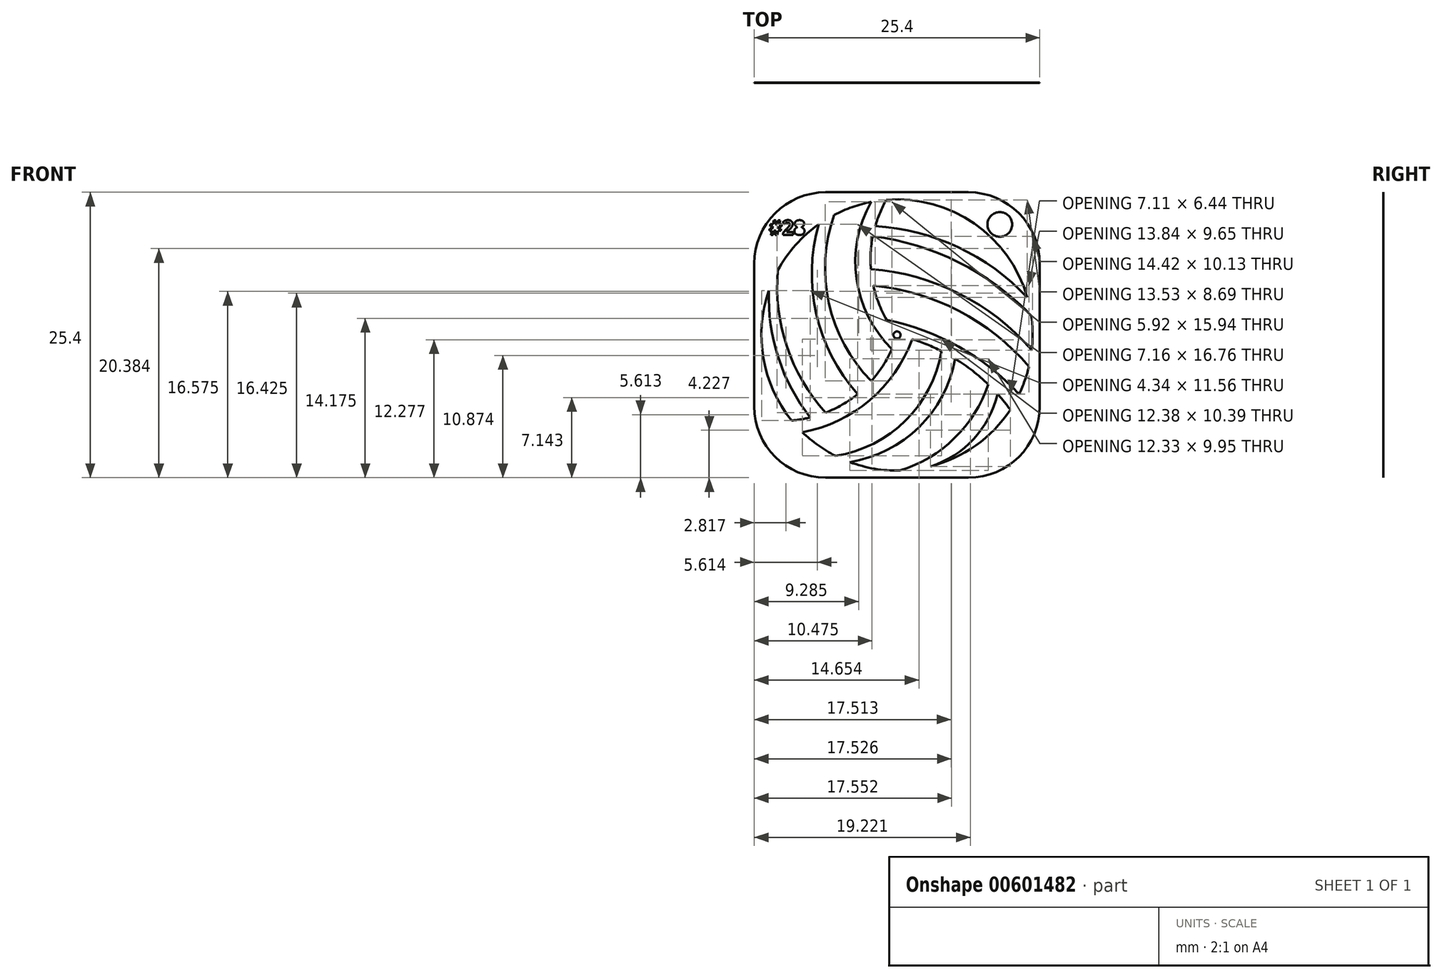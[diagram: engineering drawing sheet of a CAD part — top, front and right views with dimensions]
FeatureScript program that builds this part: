
annotation { "Feature Type Name" : "Feature", "Feature Type Description" : "" }
export const myFeature = defineFeature(function(context is Context, id is Id, definition is map)
    precondition{}
    {
        {
            var Q0;
            Q0=qCreatedBy(makeId("Front.planeOp"),FACE);
            var sketch = newSketch(context, id + "F0", { "sketchPlane" : qUnion([Q0])});
            skLineSegment(sketch, "E0", {"start": v(0, 6.35) * mm, "end": v(0, 19.05) * mm});
            skLineSegment(sketch, "E1", {"start": v(6.35, 0) * mm, "end": v(19.05, 0) * mm});
            skLineSegment(sketch, "E2", {"start": v(25.4, 6.35) * mm, "end": v(25.4, 19.05) * mm});
            skLineSegment(sketch, "E3", {"start": v(19.05, 25.4) * mm, "end": v(6.35, 25.4) * mm});
            skCircle(sketch, "E4", {"center": v(12.7, 12.7) * mm, "radius": 12.07 * mm});
            skPoint(sketch, "E5.visualSharp", {"position": v(0, 25.4) * mm});
            skArc(sketch, "E5.filletArc", {"start": v(6.35, 25.4) * mm, "mid": v(1.86, 23.54) * mm, "end": v(0, 19.05) * mm});
            skPoint(sketch, "E6.visualSharp", {"position": v(0, 0) * mm});
            skArc(sketch, "E6.filletArc", {"start": v(0, 6.35) * mm, "mid": v(1.86, 1.86) * mm, "end": v(6.35, 0) * mm});
            skPoint(sketch, "E7.visualSharp", {"position": v(25.4, 0) * mm});
            skArc(sketch, "E7.filletArc", {"start": v(19.05, 0) * mm, "mid": v(23.54, 1.86) * mm, "end": v(25.4, 6.35) * mm});
            skPoint(sketch, "E8.visualSharp", {"position": v(25.4, 25.4) * mm});
            skArc(sketch, "E8.filletArc", {"start": v(25.4, 19.05) * mm, "mid": v(23.54, 23.54) * mm, "end": v(19.05, 25.4) * mm});
            skPoint(sketch, "E9.centerSnap0", {"position": v(23.54, 23.54) * mm});
            skCircle(sketch, "E10", {"center": v(21.84, 22.54) * mm, "radius": 1.1 * mm});
            skPoint(sketch, "E9.center.orphan", {"position": v(21.97, 23.54) * mm});
            skArc(sketch, "E11", {"start": v(11.75, 24.73) * mm, "mid": v(10.37, 18.57) * mm, "end": v(12.7, 12.7) * mm});
            skArc(sketch, "E12", {"start": v(22.78, 6.06) * mm, "mid": v(18.34, 10.3) * mm, "end": v(12.7, 12.7) * mm});
            skArc(sketch, "E13", {"start": v(3.33, 5.1) * mm, "mid": v(9.2, 7.45) * mm, "end": v(12.7, 12.7) * mm});
            skLineSegment(sketch, "E14", {"start": v(15.68, 24.4) * mm, "end": v(15.68, 24.4) * mm});
            skPoint(sketch, "E15.start.orphan", {"position": v(19.05, 22.96) * mm});
            skArc(sketch, "E16", {"start": v(7.22, 1.95) * mm, "mid": v(13.45, 5.08) * mm, "end": v(16.67, 11.26) * mm});
            skArc(sketch, "E17", {"start": v(12.96, 0.64) * mm, "mid": v(17.81, 3.52) * mm, "end": v(20.82, 8.3) * mm});
            skArc(sketch, "E18", {"start": v(24.43, 9.9) * mm, "mid": v(18.2, 14.84) * mm, "end": v(10.6, 17.1) * mm});
            skArc(sketch, "E19", {"start": v(24.64, 14.44) * mm, "mid": v(18.2, 19.17) * mm, "end": v(10.54, 21.5) * mm});
            skArc(sketch, "E20", {"start": v(7.1, 23.4) * mm, "mid": v(6.64, 15.53) * mm, "end": v(10.4, 8.6) * mm});
            skArc(sketch, "E21", {"start": v(2.1, 18.46) * mm, "mid": v(2.9, 11.68) * mm, "end": v(6.35, 5.8) * mm});
            skArc(sketch, "E22", {"start": v(10.4, 24.54) * mm, "mid": v(9.1, 17.69) * mm, "end": v(12.25, 11.46) * mm});
            skArc(sketch, "E23", {"start": v(5.74, 22.56) * mm, "mid": v(5.52, 14.56) * mm, "end": v(9.2, 7.45) * mm});
            skArc(sketch, "E24", {"start": v(1.3, 16.65) * mm, "mid": v(2.14, 10.68) * mm, "end": v(4.99, 5.36) * mm});
            skArc(sketch, "E25", {"start": v(23.56, 7.45) * mm, "mid": v(18.19, 11.67) * mm, "end": v(11.78, 14.04) * mm});
            skArc(sketch, "E26", {"start": v(24.7, 11.36) * mm, "mid": v(18.24, 16.38) * mm, "end": v(10.37, 18.57) * mm});
            skArc(sketch, "E27", {"start": v(4.28, 4.05) * mm, "mid": v(10.27, 6.9) * mm, "end": v(14.04, 12.34) * mm});
            skArc(sketch, "E28", {"start": v(8.49, 1.4) * mm, "mid": v(14.65, 4.5) * mm, "end": v(17.87, 10.59) * mm});
            skArc(sketch, "E29", {"start": v(15.67, 1) * mm, "mid": v(19.5, 3.44) * mm, "end": v(21.65, 7.45) * mm});
            skPoint(sketch, "E30.start.orphan", {"position": v(24.3, 16.04) * mm});
            skArc(sketch, "E31", {"start": v(24.3, 16.04) * mm, "mid": v(18.13, 20.5) * mm, "end": v(10.76, 22.38) * mm});
            skCircle(sketch, "E32", {"center": v(12.7, 12.7) * mm, "radius": 0.32 * mm});
            skText(sketch, "E33", { "text": "#28", "fontName": "OpenSans-Bold.ttf"});
            skLineSegment(sketch, "E34", {"start": v(0.36, 21.14) * mm, "end": v(0.36, 5.6) * mm});
            skLineSegment(sketch, "E35", {"start": v(0.36, 17.45) * mm, "end": v(0, 17.45) * mm});
            const initialGuessF0  = {"E33": [0.00131, 0.02162, 1, 0, 0.0013]};
            skSetInitialGuess(sketch, initialGuessF0);
            skSolve(sketch);
        }
        {
            var Q0;
            Q0=qSketchRegion(id+"F0",true);
            extrude(context, id + "F1", {"entities" : qUnion([Q0]), "depth" : 1 / 203.2 * mm, "offsetDistance" : 25.4 * mm});
        }
        {
            var Q0;
            Q0=qSketchRegion(id+"F0",true);
            var Q1;
            {var subQ0=sQuery(id+"F0.wireOp",EDGE,"E20");Q1=makeQuery(id+"F0.imprint","IMPRINT",FACE,{"disambiguationData":[TD([[makeQuery(id+"F0.imprint","IMPRINT",EDGE,{"derivedFrom":subQ0}),-1.0]])]});}
            var Q2;
            {var subQ0=sQuery(id+"F0.wireOp",EDGE,"E21");Q2=makeQuery(id+"F0.imprint","IMPRINT",FACE,{"disambiguationData":[TD([[makeQuery(id+"F0.imprint","IMPRINT",EDGE,{"derivedFrom":subQ0}),-1.0]])]});}
            var Q3;
            {var subQ3=sQuery(id+"F0.wireOp",EDGE,"E22");Q3=makeQuery(id+"F0.imprint","IMPRINT",FACE,{"disambiguationData":[TD([[makeQuery(id+"F0.imprint","IMPRINT",EDGE,{"derivedFrom":subQ3}),1.0]])]});}
            var Q4;
            {var subQ5=sQuery(id+"F0.wireOp",EDGE,"E25");Q4=makeQuery(id+"F0.imprint","IMPRINT",FACE,{"disambiguationData":[TD([[makeQuery(id+"F0.imprint","IMPRINT",EDGE,{"derivedFrom":subQ5}),1.0]])]});}
            var Q5;
            {var subQ7=sQuery(id+"F0.wireOp",EDGE,"E27");Q5=makeQuery(id+"F0.imprint","IMPRINT",FACE,{"disambiguationData":[TD([[makeQuery(id+"F0.imprint","IMPRINT",EDGE,{"derivedFrom":subQ7}),1.0]])]});}
            var Q6;
            {var subQ0=sQuery(id+"F0.wireOp",EDGE,"E18");Q6=makeQuery(id+"F0.imprint","IMPRINT",FACE,{"disambiguationData":[TD([[makeQuery(id+"F0.imprint","IMPRINT",EDGE,{"derivedFrom":subQ0}),-1.0]])]});}
            var Q7;
            {var subQ0=sQuery(id+"F0.wireOp",EDGE,"E19");Q7=makeQuery(id+"F0.imprint","IMPRINT",FACE,{"disambiguationData":[TD([[makeQuery(id+"F0.imprint","IMPRINT",EDGE,{"derivedFrom":subQ0}),-1.0]])]});}
            var Q8;
            {var subQ0=sQuery(id+"F0.wireOp",EDGE,"E16");Q8=makeQuery(id+"F0.imprint","IMPRINT",FACE,{"disambiguationData":[TD([[makeQuery(id+"F0.imprint","IMPRINT",EDGE,{"derivedFrom":subQ0}),-1.0]])]});}
            var Q9;
            {var subQ0=sQuery(id+"F0.wireOp",EDGE,"E17");Q9=makeQuery(id+"F0.imprint","IMPRINT",FACE,{"disambiguationData":[TD([[makeQuery(id+"F0.imprint","IMPRINT",EDGE,{"derivedFrom":subQ0}),-1.0]])]});}
            extrude(context, id + "F2", {"entities" : qUnion([Q0, Q1, Q2, Q3, Q4, Q5, Q6, Q7, Q8, Q9]), "operationType" : NewBodyOperationType.ADD, "depth" : 1 / 203.2 * mm, "offsetDistance" : 25.4 * mm});
        }
        {
            var Q0;
            Q0=makeQuery(id+"F1.opExtrude","SWEPT_FACE",FACE,{"disambiguationData":[OSD([sQuery(id+"F0.wireOp",EDGE,"E0")])]});
            var sketch = newSketch(context, id + "F3", { "sketchPlane" : qUnion([Q0])});
            skText(sketch, "E36", { "text": "T", "fontName": "OpenSans-Bold.ttf"});
            skText(sketch, "E37", { "text": "E", "fontName": "OpenSans-Bold.ttf"});
            skText(sketch, "E38", { "text": "M", "fontName": "OpenSans-Bold.ttf"});
            skText(sketch, "E39", { "text": "A", "fontName": "OpenSans-Bold.ttf"});
            const initialGuessF3  = {"E36": [0.00092, 0.01462, 1, 0, 0.00141], "E37": [0.00102, 0.01293, 1, 0, 0.00135], "E38": [0.00067, 0.00942, 1, 0, 0.00142], "E39": [0.0008, 0.01112, 1, 0, 0.00145]};
            skSetInitialGuess(sketch, initialGuessF3);
            skSolve(sketch);
        }
        {
            var Q0;
            Q0=qSketchRegion(id+"F3",true);
            extrude(context, id + "F4", {"entities" : qUnion([Q0]), "operationType" : NewBodyOperationType.REMOVE, "oppositeDirection" : true, "depth" : 0.36 * mm, "offsetDistance" : 25.4 * mm});
        }
        {
            var Q0;
            Q0=makeQuery(id+"F1.opExtrude","SWEPT_FACE",FACE,{"disambiguationData":[OSD([sQuery(id+"F0.wireOp",EDGE,"E2")])]});
            var sketch = newSketch(context, id + "F5", { "sketchPlane" : qUnion([Q0])});
            skText(sketch, "E40", { "text": "M", "fontName": "OpenSans-Bold.ttf"});
            skText(sketch, "E41", { "text": "A", "fontName": "OpenSans-Bold.ttf"});
            skText(sketch, "E42", { "text": "G", "fontName": "OpenSans-Bold.ttf"});
            skText(sketch, "E43", { "text": "A", "fontName": "OpenSans-Bold.ttf"});
            skText(sketch, "E44", { "text": "E", "fontName": "OpenSans-Bold.ttf"});
            skText(sketch, "E45", { "text": "N", "fontName": "OpenSans-Bold.ttf"});
            skText(sketch, "E46", { "text": "R", "fontName": "OpenSans-Bold.ttf"});
            skPoint(sketch, "E46.secondSnap0", {"position": v(-0.88, 14.58) * mm});
            const initialGuessF5  = {"E40": [-0.00252, 0.0175, 1, 0, 0.00155], "E41": [-0.00227, 0.01568, 1, 0, 0.0015], "E42": [-0.00245, 0.00995, 1, 0, 0.00164], "E43": [-0.00245, 0.01195, 1, 0, 0.00167], "E44": [-0.00224, 0.00828, 1, 0, 0.00141], "E45": [-0.00232, 0.01392, 1, 0, 0.00131], "E46": [-0.0023, 0.0066, 1, 0, 0.0014]};
            skSetInitialGuess(sketch, initialGuessF5);
            skSolve(sketch);
        }
        {
            var Q0;
            Q0=qSketchRegion(id+"F5",true);
            extrude(context, id + "F6", {"entities" : qUnion([Q0]), "operationType" : NewBodyOperationType.REMOVE, "oppositeDirection" : true, "depth" : 0.36 * mm, "offsetDistance" : 25.4 * mm});
        }
    });
